# Revit family: LeL Metope 3.1
name_source: partatom
category: Lighting Fixtures
units: mm (PartAtom-declared; Revit-internal decimal feet)

## family parameters
Cut with Voids When Loaded = Yes
Host = Face
Light Source = No
Part Type = Normal
Room Calculation Point = No
Round Connector Dimension = Use Diameter
Shared = No

## types (12) — shared parameters
CCT = 3000 K
CRI = 80
Default Elevation = 1219 mm
Description = Outdoor Wall Mounted
Height = 100 mm  [stored 0.328084 ft]
IK = IK05
IP = IP65
Lamp = LED
Lenght = 55 mm  [stored 0.180446 ft]
Manufacturer = L&L Luce&Light
Model = TM31
URL = https://www.lucelight.it
Weight = 2.00 kg
Widht = 15 mm  [stored 0.0492126 ft]

## per-type parameters (varying)
| type | Alimentazione | Apparent Load | Lumen Output | Photometry2 | Rated Power supply | Wattage |
| 3.1 A 10W 24Vdc | 24 V | 10 VA | 670 lm | TM3 Light source : 3.1 A 10W 24Vdc | 24 V | 10 W |
| 3.1 A 12W 110-230Vac | 230 V | 12 VA | 670 lm | TM3 Light source : 3.1 A 12W 110-230Vac | 230 V | 12 W |
| 3.1 D 10W 24Vdc | 24 V | 10 VA | 630 lm | TM3 Light source : 3.1 D 10W 24Vdc | 24 V | 10 W |
| 3.1 D 12W 230Vac | 230 V | 12 VA | 630 lm | TM3 Light source : 3.1 D 12W 110-230Vac | 230 V | 12 W |
| 3.1 K 54° 10W 24Vdc | 24 V | 10 VA | 691 lm | TM3 Light source : 3.1 K 54° 10W 24Vdc | 24 V | 10 W |
| 3.1 K 54° 12W 110-230Vac | 230 V | 12 VA | 691 lm | TM3 Light source : 3.1 K 54° 12W 110-230Vac | 230 V | 12 W |
| 3.1 L 37° 10W 24Vdc | 24 V | 10 VA | 691 lm | TM3 Light source : 3.1 L 37° 10W 24Vdc | 24 V | 10 W |
| 3.1 L 37° 12W 110-230Vac | 230 V | 12 VA | 685 lm | TM3 Light source : 3.1 L 37° 12W 110-230Vac | 230 V | 12 W |
| 3.1 M 26° 10W 24Vdc | 24 V | 10 VA | 751 lm | TM3 Light source : 3.1 M 26° 10W 24Vdc | 24 V | 10 W |
| 3.1 M 26° 12W 110-230Vac | 230 V | 12 VA | 751 lm | TM3 Light source : 3.1 M 26° 12W 110-230Vac | 230 V | 12 W |
| 3.1 S 16° 10W 24Vdc | 24 V | 10 VA | 761 lm | TM3 Light source : 3.1 S 16° 10W 24Vdc | 24 V | 10 W |
| 3.1 S 16° 12W 110-230Vac | 230 V | 12 VA | 761 lm | TM3 Light source : 3.1 S 16° 12W 110-230Vac | 230 V | 12 W |

note: [stored X ft] marks values corroborated as IEEE doubles in the binary element streams (Revit-internal decimal feet)
